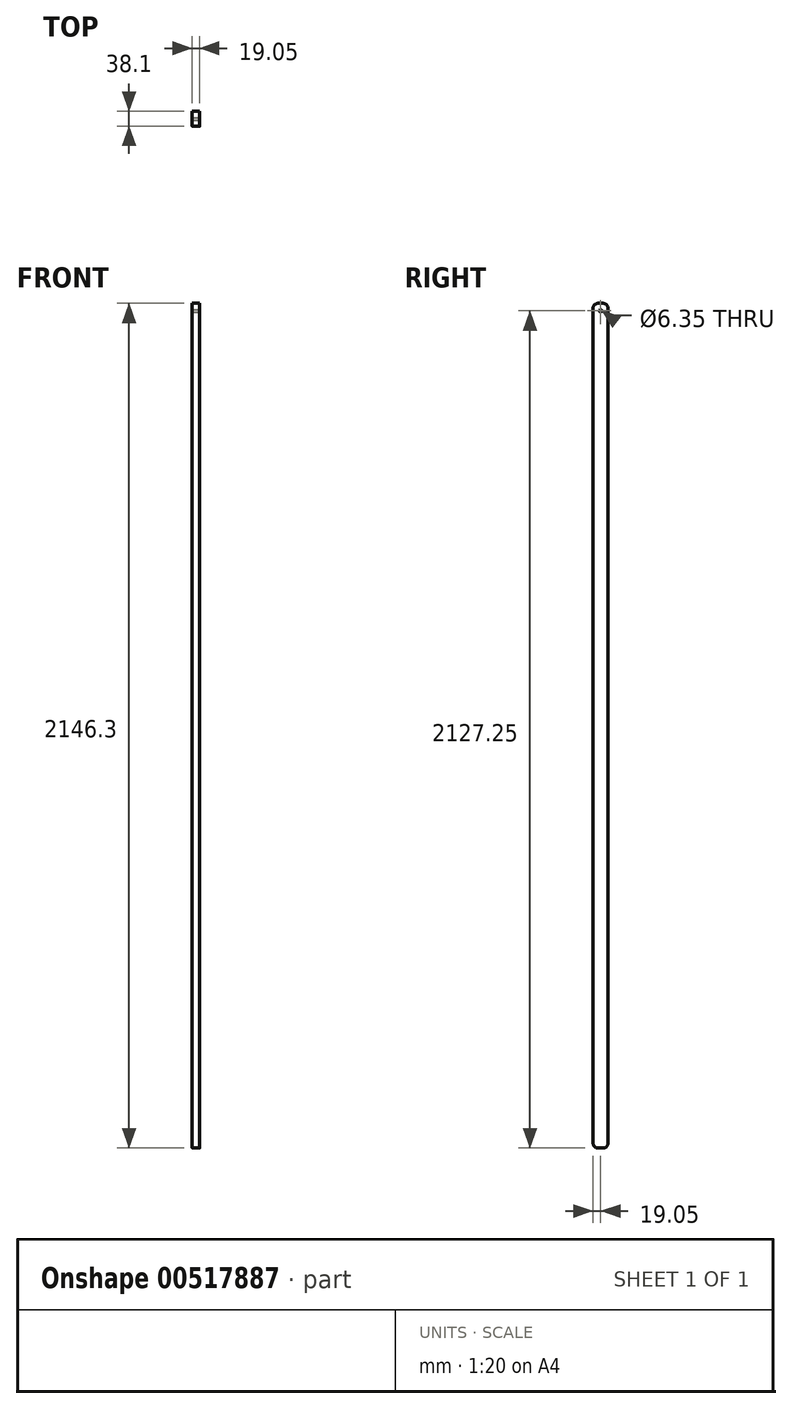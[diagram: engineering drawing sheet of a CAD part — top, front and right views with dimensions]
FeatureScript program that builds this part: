
annotation { "Feature Type Name" : "Feature", "Feature Type Description" : "" }
export const myFeature = defineFeature(function(context is Context, id is Id, definition is map)
    precondition{}
    {
        {
            var Q0;
            Q0=qCreatedBy(makeId("Top.planeOp"),FACE);
            var sketch = newSketch(context, id + "F0", { "sketchPlane" : qUnion([Q0])});
            skLineSegment(sketch, "E0.bottom", {"start": v(0, 0) * mm, "end": v(19.05, 0) * mm});
            skLineSegment(sketch, "E0.top", {"start": v(0, 38.1) * mm, "end": v(19.05, 38.1) * mm});
            skLineSegment(sketch, "E0.left", {"start": v(0, 0) * mm, "end": v(0, 38.1) * mm});
            skLineSegment(sketch, "E0.right", {"start": v(19.05, 0) * mm, "end": v(19.05, 38.1) * mm});
            skLineSegment(sketch, "E1.0", {"start": v(3.17, 34.92) * mm, "end": v(15.87, 34.92) * mm, "construction": true});
            skLineSegment(sketch, "E1.1", {"start": v(3.18, 3.18) * mm, "end": v(3.17, 34.92) * mm, "construction": true});
            skLineSegment(sketch, "E1.2", {"start": v(3.18, 3.18) * mm, "end": v(15.87, 3.18) * mm, "construction": true});
            skLineSegment(sketch, "E1.3", {"start": v(15.87, 3.17) * mm, "end": v(15.87, 34.92) * mm, "construction": true});
            skSolve(sketch);
        }
        {
            var Q0;
            Q0 = qSketchRegion(id + "F0", true);
            extrude(context, id + "F1", {"entities" : qUnion([Q0]), "oppositeDirection" : true, "depth" : 2146.3 * mm, "offsetDistance" : 25.4 * mm});
        }
        {
            var Q0;
            Q0=makeQuery(id+"F1.opExtrude","SWEPT_FACE",FACE,{"disambiguationData":[OSD([sQuery(id+"F0.wireOp",EDGE,"E0.right")])]});
            var sketch = newSketch(context, id + "F2", { "sketchPlane" : qUnion([Q0])});
            skCircle(sketch, "E2", {"center": v(19.05, 0) * mm, "radius": 3.18 * mm, "construction": true});
            skCircle(sketch, "E3.0.1.0", {"center": v(19.05, -19.05) * mm, "radius": 3.18 * mm});
            skLineSegment(sketch, "E3.direction1", {"start": v(19.05, 0) * mm, "end": v(38.1, 0) * mm, "construction": true});
            skLineSegment(sketch, "E3.direction2", {"start": v(19.05, 0) * mm, "end": v(19.05, -19.05) * mm, "construction": true});
            skSolve(sketch);
        }
        {
            var Q0;
            Q0=makeQuery(id+"F2.imprint","IMPRINT",FACE,{"disambiguationData":[TD([[makeQuery(id+"F2.imprint","IMPRINT",EDGE,{"derivedFrom":sQuery(id+"F2.wireOp",EDGE,"E3.0.1.0")}),1.0]])]});
            var Q1;
            Q1=sQuery(id+"F2.wireOp",EDGE,"E2");
            extrude(context, id + "F3", {"entities" : qUnion([Q0]), "operationType" : NewBodyOperationType.REMOVE, "surfaceEntities" : qUnion([Q1]), "endBound" : BoundingType.THROUGH_ALL, "oppositeDirection" : true, "depth" : 25.4 * mm, "offsetDistance" : 25.4 * mm});
        }
        {
            var Q0;
            Q0=makeQuery(id+"F1.opExtrude","CAP_EDGE",EDGE,{"disambiguationData":[OSD([sQuery(id+"F0.wireOp",EDGE,"E0.bottom")])],"isStart":true});
            var Q1;
            Q1=makeQuery(id+"F1.opExtrude","CAP_EDGE",EDGE,{"disambiguationData":[OSD([sQuery(id+"F0.wireOp",EDGE,"E0.top")])],"isStart":true});
            var Q2;
            Q2=makeQuery(id+"F1.opExtrude","CAP_EDGE",EDGE,{"disambiguationData":[OSD([sQuery(id+"F0.wireOp",EDGE,"E0.bottom")])],"isStart":false});
            var Q3;
            Q3=makeQuery(id+"F1.opExtrude","CAP_EDGE",EDGE,{"disambiguationData":[OSD([sQuery(id+"F0.wireOp",EDGE,"E0.top")])],"isStart":false});
            fillet(context, id + "F4", {"entities" : qUnion([Q0, Q1, Q2, Q3]), "radius" : 12.7 * mm, "tangentPropagation" : true, "allowEdgeOverflow" : false});
        }
    });
